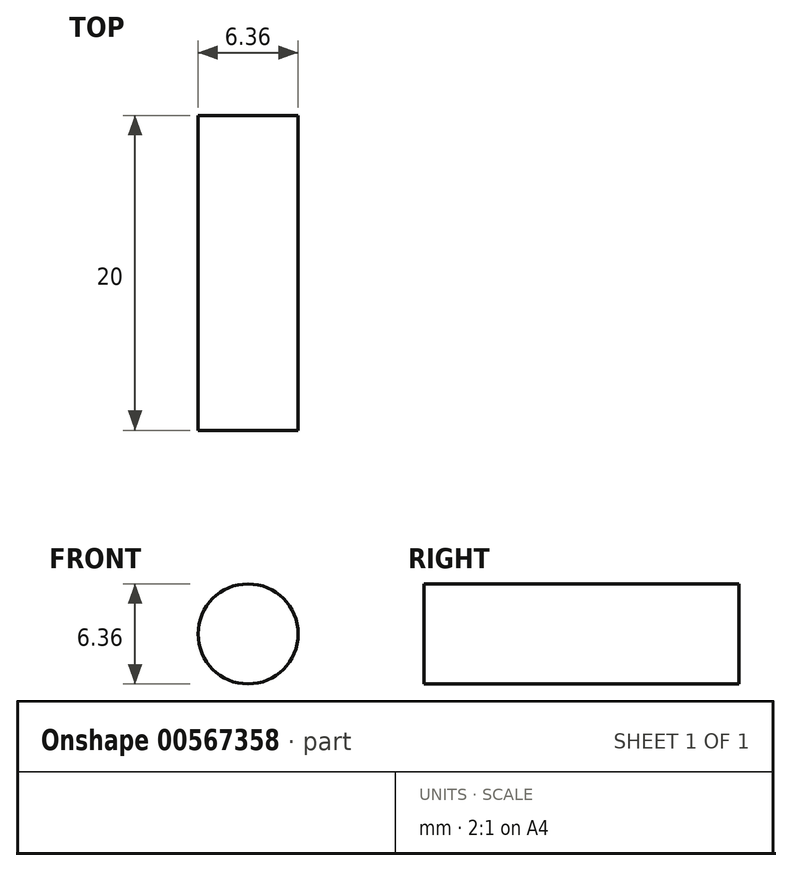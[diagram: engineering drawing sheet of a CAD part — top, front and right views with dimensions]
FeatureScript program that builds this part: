
annotation { "Feature Type Name" : "Feature", "Feature Type Description" : "" }
export const myFeature = defineFeature(function(context is Context, id is Id, definition is map)
    precondition{}
    {
        {
            var Q0;
            Q0=qCreatedBy(makeId("Front.planeOp"),FACE);
            var sketch = newSketch(context, id + "F0", { "sketchPlane" : qUnion([Q0])});
            skCircle(sketch, "E0", {"center": v(0, 0) * mm, "radius": 3.18 * mm});
            skSolve(sketch);
        }
        {
            var Q0;
            Q0 = qSketchRegion(id + "F0", true);
            extrude(context, id + "F1", {"entities" : qUnion([Q0]), "depth" : 20 * mm, "offsetDistance" : 25 * mm});
        }
    });
